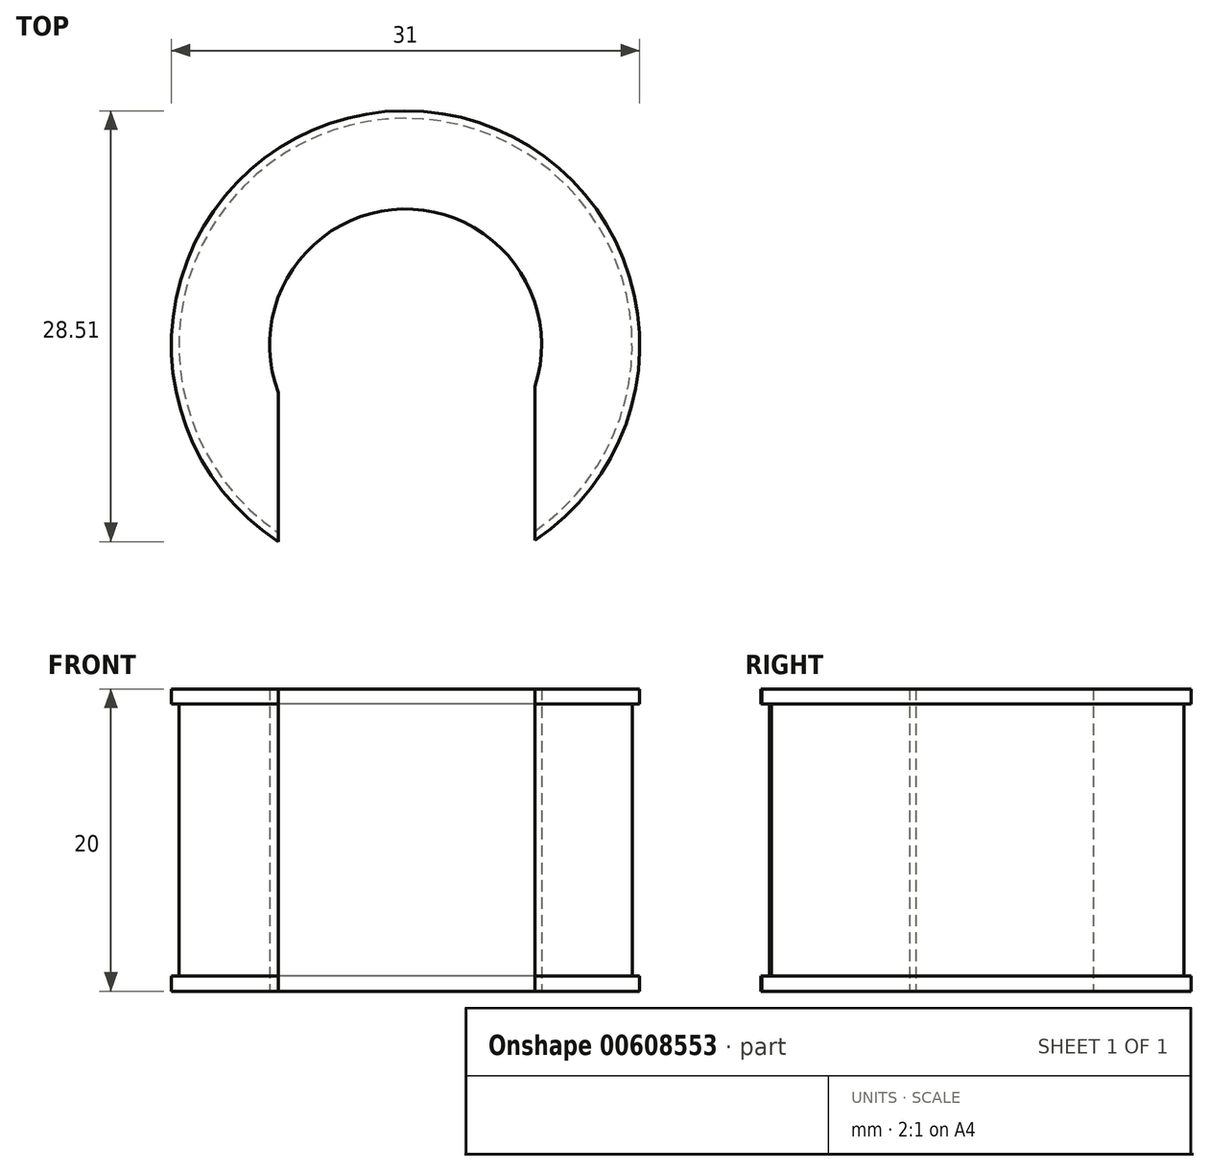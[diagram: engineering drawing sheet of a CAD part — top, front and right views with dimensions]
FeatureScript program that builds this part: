
annotation { "Feature Type Name" : "Feature", "Feature Type Description" : "" }
export const myFeature = defineFeature(function(context is Context, id is Id, definition is map)
    precondition{}
    {
        {
            var Q0;
            Q0=qCreatedBy(makeId("Top.planeOp"),FACE);
            var sketch = newSketch(context, id + "F0", { "sketchPlane" : qUnion([Q0])});
            skCircle(sketch, "E0", {"center": v(0, 0) * mm, "radius": 9 * mm});
            skCircle(sketch, "E1", {"center": v(0, 0) * mm, "radius": 15 * mm});
            skLineSegment(sketch, "E2.bottom", {"start": v(-9, 0) * mm, "end": v(8.57, 0) * mm});
            skLineSegment(sketch, "E2.top", {"start": v(-8.43, -18.63) * mm, "end": v(8.57, -18.63) * mm});
            skLineSegment(sketch, "E2.left", {"start": v(-8.43, 0) * mm, "end": v(-8.43, -18.63) * mm});
            skLineSegment(sketch, "E2.right", {"start": v(8.57, 0) * mm, "end": v(8.57, -18.63) * mm});
            skCircle(sketch, "E3", {"center": v(0, 0) * mm, "radius": 15.5 * mm});
            skSolve(sketch);
        }
        {
            var Q0;
            Q0=makeQuery(id+"F0.imprint","IMPRINT",FACE,{"disambiguationData":[TD([[makeQuery(id+"F0.imprint","IMPRINT",EDGE,{"derivedFrom":sQuery(id+"F0.wireOp",EDGE,"E0")}),-1.0]])]});
            extrude(context, id + "F1", {"entities" : qUnion([Q0]), "depth" : 20 * mm, "offsetDistance" : 25 * mm});
        }
        {
            var Q0;
            {var subQ0=sQuery(id+"F0.wireOp",EDGE,"E2.left");var subQ1=sQuery(id+"F0.wireOp",EDGE,"E1");var subQ2=makeQuery(id+"F0.imprint","INTERSECT",VERTEX,{"derivedFrom":[subQ1,subQ0]});Q0=makeQuery(id+"F0.imprint","IMPRINT",FACE,{"disambiguationData":[TD([[makeQuery(id+"F0.imprint","IMPRINT",EDGE,{"disambiguationData":[TD([[subQ2,1.0]])],"derivedFrom":subQ1}),-1.0]])]});}
            extrude(context, id + "F2", {"entities" : qUnion([Q0]), "operationType" : NewBodyOperationType.ADD, "depth" : 1 * mm, "offsetDistance" : 25 * mm});
        }
        {
            var Q0;
            {var subQ0=sQuery(id+"F0.wireOp",EDGE,"E2.left");var subQ1=sQuery(id+"F0.wireOp",EDGE,"E1");var subQ2=makeQuery(id+"F0.imprint","INTERSECT",VERTEX,{"derivedFrom":[subQ1,subQ0]});Q0=makeQuery(id+"F0.imprint","IMPRINT",FACE,{"disambiguationData":[TD([[makeQuery(id+"F0.imprint","IMPRINT",EDGE,{"disambiguationData":[TD([[subQ2,1.0]])],"derivedFrom":subQ1}),-1.0]])]});}
            var Q1;
            Q1=makeQuery(id+"F1.opExtrude","CAP_FACE",FACE,{"disambiguationData":[OSD([sQuery(id+"F0.wireOp",EDGE,"E0"),sQuery(id+"F0.wireOp",EDGE,"E1"),sQuery(id+"F0.wireOp",EDGE,"E2.left"),sQuery(id+"F0.wireOp",EDGE,"E2.right")])],"isStart":false});
            extrude(context, id + "F3", {"entities" : qUnion([Q0]), "operationType" : NewBodyOperationType.ADD, "endBound" : BoundingType.UP_TO_SURFACE, "depth" : 20 * mm, "endBoundEntityFace" : qUnion([Q1]), "offsetDistance" : 25 * mm, "hasSecondDirection" : true, "secondDirectionOppositeDirection" : false, "secondDirectionDepth" : 19 * mm});
        }
    });
